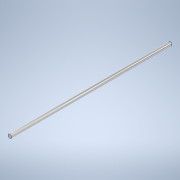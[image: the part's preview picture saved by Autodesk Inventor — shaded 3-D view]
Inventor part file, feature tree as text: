
AUTODESK INVENTOR PART (.ipt)
format: ipt  version: 2020.3 (Build 243373000, 373)  size: 93,184 bytes
history: native  units: mm
features: extrude x1, sketch x1
ambient origin geometry x8: Origin, YZ Plane, XZ Plane, XY Plane, X Axis, Y Axis, Z Axis, Center Point
bodies: Solid1 (feature_tree)
feature tree (2):
  extrude  "Extrusion1"  Depth=280.0mm TaperAngle=0.0deg
  sketch  "Sketch1"  dims[d0=6.5mm d1=280.0mm d2=0.0mm]
